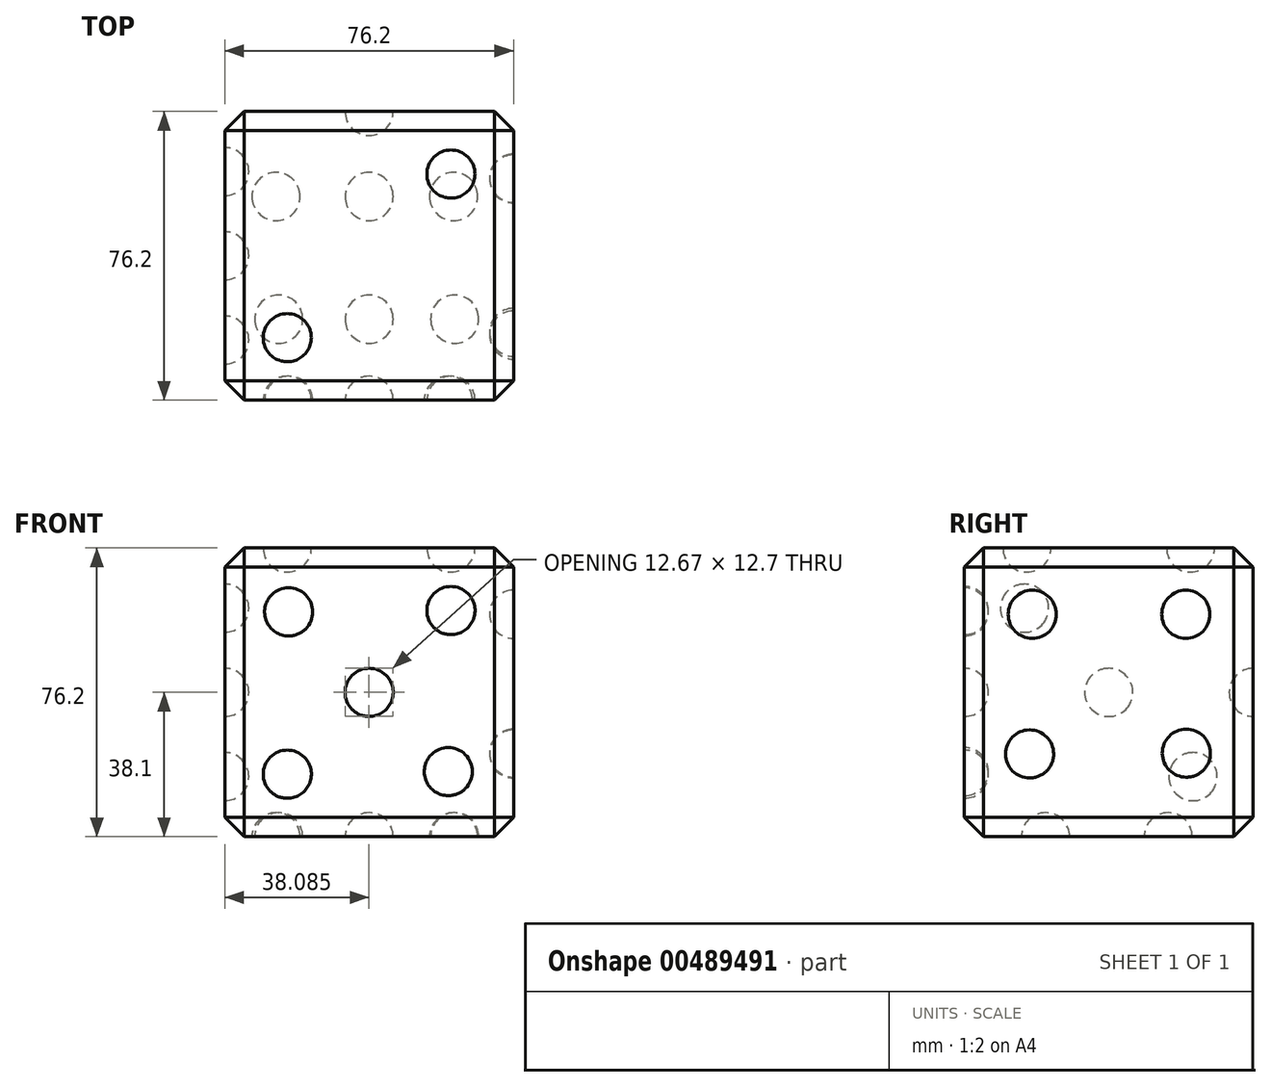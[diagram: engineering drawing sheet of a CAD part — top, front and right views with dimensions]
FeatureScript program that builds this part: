
annotation { "Feature Type Name" : "Feature", "Feature Type Description" : "" }
export const myFeature = defineFeature(function(context is Context, id is Id, definition is map)
    precondition{}
    {
        {
            var Q0;
            Q0=qCreatedBy(makeId("Top.planeOp"),FACE);
            var sketch = newSketch(context, id + "F0", { "sketchPlane" : qUnion([Q0])});
            skLineSegment(sketch, "E0", {"start": v(0, 0) * mm, "end": v(-76.2, 0) * mm});
            skLineSegment(sketch, "E1", {"start": v(-76.2, 0) * mm, "end": v(-76.2, 76.2) * mm});
            skLineSegment(sketch, "E2", {"start": v(-76.2, 76.2) * mm, "end": v(0, 76.2) * mm});
            skLineSegment(sketch, "E3", {"start": v(0, 76.2) * mm, "end": v(0, 0) * mm});
            skSolve(sketch);
        }
        {
            var Q0;
            Q0 = qSketchRegion(id + "F0", true);
            extrude(context, id + "F1", {"entities" : qUnion([Q0]), "depth" : 76.2 * mm});
        }
        {
            var Q0;
            Q0=makeQuery(id+"F1.opExtrude","SWEPT_FACE",FACE,{"disambiguationData":[OSD([sQuery(id+"F0.wireOp",EDGE,"E2")])]});
            var sketch = newSketch(context, id + "F2", { "sketchPlane" : qUnion([Q0])});
            skLineSegment(sketch, "E4", {"start": v(38.1, 0) * mm, "end": v(38.1, 76.2) * mm});
            skArc(sketch, "E5", {"start": v(38.1, 31.75) * mm, "mid": v(44.45, 38.1) * mm, "end": v(38.1, 44.45) * mm});
            skSolve(sketch);
        }
        {
            var Q0;
            {var subQ0=sQuery(id+"F2.wireOp",EDGE,"E5");Q0=makeQuery(id+"F2.imprint","IMPRINT",FACE,{"disambiguationData":[TD([[makeQuery(id+"F2.imprint","IMPRINT",EDGE,{"derivedFrom":subQ0}),1.0]])]});}
            var Q1;
            Q1=sQuery(id+"F2.wireOp",EDGE,"E4");
            revolve(context, id + "F3", {"operationType" : NewBodyOperationType.REMOVE, "entities" : qUnion([Q0]), "axis" : qUnion([Q1]), "revolveType" : RevolveType.FULL, "oppositeDirection" : true});
        }
        {
            var Q0;
            Q0=makeQuery(id+"F1.opExtrude","SWEPT_FACE",FACE,{"disambiguationData":[OSD([sQuery(id+"F0.wireOp",EDGE,"E1")])]});
            var sketch = newSketch(context, id + "F4", { "sketchPlane" : qUnion([Q0])});
            skLineSegment(sketch, "E6", {"start": v(0, 76.2) * mm, "end": v(-76.2, 0) * mm});
            skArc(sketch, "E7", {"start": v(-42.6, 33.6) * mm, "mid": v(-33.6, 33.6) * mm, "end": v(-33.6, 42.6) * mm});
            skArc(sketch, "E8", {"start": v(-64.82, 11.38) * mm, "mid": v(-55.83, 11.38) * mm, "end": v(-55.83, 20.37) * mm});
            skArc(sketch, "E9", {"start": v(-20.37, 55.83) * mm, "mid": v(-11.38, 55.83) * mm, "end": v(-11.38, 64.82) * mm});
            skSolve(sketch);
        }
        {
            var Q0;
            {var subQ0=sQuery(id+"F4.wireOp",EDGE,"E7");Q0=makeQuery(id+"F4.imprint","IMPRINT",FACE,{"disambiguationData":[TD([[makeQuery(id+"F4.imprint","IMPRINT",EDGE,{"derivedFrom":subQ0}),1.0]])]});}
            var Q1;
            {var subQ0=sQuery(id+"F4.wireOp",EDGE,"E9");Q1=makeQuery(id+"F4.imprint","IMPRINT",FACE,{"disambiguationData":[TD([[makeQuery(id+"F4.imprint","IMPRINT",EDGE,{"derivedFrom":subQ0}),1.0]])]});}
            var Q2;
            {var subQ0=sQuery(id+"F4.wireOp",EDGE,"E8");Q2=makeQuery(id+"F4.imprint","IMPRINT",FACE,{"disambiguationData":[TD([[makeQuery(id+"F4.imprint","IMPRINT",EDGE,{"derivedFrom":subQ0}),1.0]])]});}
            var Q3;
            Q3=sQuery(id+"F4.wireOp",EDGE,"E6");
            revolve(context, id + "F5", {"operationType" : NewBodyOperationType.REMOVE, "entities" : qUnion([Q0, Q1, Q2]), "axis" : qUnion([Q3]), "revolveType" : RevolveType.FULL, "oppositeDirection" : true});
        }
        {
            var Q0;
            Q0=makeQuery(id+"F1.opExtrude","CAP_FACE",FACE,{"disambiguationData":[OSD([sQuery(id+"F0.wireOp",EDGE,"E0"),sQuery(id+"F0.wireOp",EDGE,"E1"),sQuery(id+"F0.wireOp",EDGE,"E2"),sQuery(id+"F0.wireOp",EDGE,"E3")])],"isStart":false});
            var sketch = newSketch(context, id + "F6", { "sketchPlane" : qUnion([Q0])});
            skLineSegment(sketch, "E10", {"start": v(0, 0) * mm, "end": v(-76.2, 76.2) * mm});
            skLineSegment(sketch, "E11", {"start": v(-76.2, 0) * mm, "end": v(0, 76.2) * mm});
            skArc(sketch, "E12", {"start": v(-55.2, 21) * mm, "mid": v(-64.18, 21) * mm, "end": v(-64.18, 12.02) * mm});
            skArc(sketch, "E13", {"start": v(-12.02, 12.02) * mm, "mid": v(-12.02, 21) * mm, "end": v(-21, 21) * mm});
            skArc(sketch, "E14", {"start": v(-42.6, 42.6) * mm, "mid": v(-44.45, 38.1) * mm, "end": v(-42.6, 33.6) * mm});
            skArc(sketch, "E15", {"start": v(-12.02, 64.18) * mm, "mid": v(-21, 64.18) * mm, "end": v(-21, 55.2) * mm});
            skArc(sketch, "E16", {"start": v(-55.2, 55.2) * mm, "mid": v(-55.2, 64.18) * mm, "end": v(-64.18, 64.18) * mm});
            skSolve(sketch);
        }
        {
            var Q0;
            {var subQ0=sQuery(id+"F6.wireOp",EDGE,"E12");Q0=makeQuery(id+"F6.imprint","IMPRINT",FACE,{"disambiguationData":[TD([[makeQuery(id+"F6.imprint","IMPRINT",EDGE,{"derivedFrom":subQ0}),1.0]])]});}
            var Q1;
            {var subQ0=sQuery(id+"F6.wireOp",EDGE,"E15");Q1=makeQuery(id+"F6.imprint","IMPRINT",FACE,{"disambiguationData":[TD([[makeQuery(id+"F6.imprint","IMPRINT",EDGE,{"derivedFrom":subQ0}),1.0]])]});}
            var Q2;
            Q2=sQuery(id+"F6.wireOp",EDGE,"E11");
            revolve(context, id + "F7", {"operationType" : NewBodyOperationType.REMOVE, "entities" : qUnion([Q0, Q1]), "axis" : qUnion([Q2]), "revolveType" : RevolveType.FULL, "oppositeDirection" : true});
        }
        {
            var Q0;
            Q0=makeQuery(id+"F1.opExtrude","SWEPT_FACE",FACE,{"disambiguationData":[OSD([sQuery(id+"F0.wireOp",EDGE,"E0")])]});
            var sketch = newSketch(context, id + "F8", { "sketchPlane" : qUnion([Q0])});
            skLineSegment(sketch, "E17", {"start": v(0, 76.2) * mm, "end": v(-76.2, 0) * mm});
            skArc(sketch, "E18", {"start": v(-12.02, 64.18) * mm, "mid": v(-21, 64.18) * mm, "end": v(-21, 55.2) * mm});
            skArc(sketch, "E19", {"start": v(-64.18, 12.02) * mm, "mid": v(-55.2, 12.02) * mm, "end": v(-55.2, 21) * mm});
            skPoint(sketch, "E20.center.orphan", {"position": v(-59.69, 59.7) * mm});
            skPoint(sketch, "E21.start.orphan", {"position": v(-76.2, 76.2) * mm});
            skPoint(sketch, "E22.trimOffspring.end.orphan", {"position": v(-16.5, 16.5) * mm});
            skPoint(sketch, "E23.trimOffspring.end.orphan", {"position": v(0, 0) * mm});
            skPoint(sketch, "E24.center.orphan", {"position": v(-38.1, 38.1) * mm});
            skArc(sketch, "E25", {"start": v(-33.6, 42.6) * mm, "mid": v(-42.6, 42.6) * mm, "end": v(-42.6, 33.6) * mm});
            skLineSegment(sketch, "E26.trimOffspring", {"start": v(-42.6, 42.6) * mm, "end": v(-38.1, 38.1) * mm});
            skSolve(sketch);
        }
        {
            var Q0;
            {var subQ0=sQuery(id+"F8.wireOp",EDGE,"E25");Q0=makeQuery(id+"F8.imprint","IMPRINT",FACE,{"disambiguationData":[TD([[makeQuery(id+"F8.imprint","IMPRINT",EDGE,{"derivedFrom":subQ0}),1.0]])]});}
            var Q1;
            {var subQ0=sQuery(id+"F8.wireOp",EDGE,"E19");Q1=makeQuery(id+"F8.imprint","IMPRINT",FACE,{"disambiguationData":[TD([[makeQuery(id+"F8.imprint","IMPRINT",EDGE,{"derivedFrom":subQ0}),1.0]])]});}
            var Q2;
            {var subQ0=sQuery(id+"F8.wireOp",EDGE,"E18");Q2=makeQuery(id+"F8.imprint","IMPRINT",FACE,{"disambiguationData":[TD([[makeQuery(id+"F8.imprint","IMPRINT",EDGE,{"derivedFrom":subQ0}),1.0]])]});}
            var Q3;
            Q3=sQuery(id+"F8.wireOp",EDGE,"E17");
            revolve(context, id + "F9", {"operationType" : NewBodyOperationType.REMOVE, "entities" : qUnion([Q0, Q1, Q2]), "axis" : qUnion([Q3]), "revolveType" : RevolveType.FULL, "oppositeDirection" : true});
        }
        {
            var Q0;
            Q0=makeQuery(id+"F1.opExtrude","SWEPT_FACE",FACE,{"disambiguationData":[OSD([sQuery(id+"F0.wireOp",EDGE,"E0")])]});
            var sketch = newSketch(context, id + "F10", { "sketchPlane" : qUnion([Q0])});
            skLineSegment(sketch, "E27", {"start": v(-76.2, 76.2) * mm, "end": v(0, 0) * mm});
            skLineSegment(sketch, "E28", {"start": v(0, 0) * mm, "end": v(-0.99, -0.3) * mm});
            skArc(sketch, "E29", {"start": v(-54.86, 54.86) * mm, "mid": v(-54.86, 63.84) * mm, "end": v(-63.84, 63.84) * mm});
            skArc(sketch, "E30", {"start": v(-12.7, 12.7) * mm, "mid": v(-12.7, 21.69) * mm, "end": v(-21.69, 21.69) * mm});
            skSolve(sketch);
        }
        {
            var Q0;
            {var subQ0=sQuery(id+"F10.wireOp",EDGE,"E29");Q0=makeQuery(id+"F10.imprint","IMPRINT",FACE,{"disambiguationData":[TD([[makeQuery(id+"F10.imprint","IMPRINT",EDGE,{"derivedFrom":subQ0}),1.0]])]});}
            var Q1;
            {var subQ0=sQuery(id+"F10.wireOp",EDGE,"E30");Q1=makeQuery(id+"F10.imprint","IMPRINT",FACE,{"disambiguationData":[TD([[makeQuery(id+"F10.imprint","IMPRINT",EDGE,{"derivedFrom":subQ0}),1.0]])]});}
            var Q2;
            Q2=sQuery(id+"F10.wireOp",EDGE,"E27");
            revolve(context, id + "F11", {"operationType" : NewBodyOperationType.REMOVE, "entities" : qUnion([Q0, Q1]), "axis" : qUnion([Q2]), "revolveType" : RevolveType.FULL, "oppositeDirection" : true});
        }
        {
            var Q0;
            Q0=makeQuery(id+"F1.opExtrude","CAP_FACE",FACE,{"disambiguationData":[OSD([sQuery(id+"F0.wireOp",EDGE,"E0"),sQuery(id+"F0.wireOp",EDGE,"E1"),sQuery(id+"F0.wireOp",EDGE,"E2"),sQuery(id+"F0.wireOp",EDGE,"E3")])],"isStart":true});
            var sketch = newSketch(context, id + "F12", { "sketchPlane" : qUnion([Q0])});
            skLineSegment(sketch, "E31", {"start": v(0, -21.4) * mm, "end": v(-76.2, -21.4) * mm});
            skPoint(sketch, "E32.center.orphan", {"position": v(-38.1, -21.4) * mm});
            skArc(sketch, "E33", {"start": v(-31.75, -21.4) * mm, "mid": v(-38.1, -15.06) * mm, "end": v(-44.45, -21.4) * mm});
            skArc(sketch, "E34", {"start": v(-9.17, -21.4) * mm, "mid": v(-15.52, -15.06) * mm, "end": v(-21.87, -21.4) * mm});
            skArc(sketch, "E35", {"start": v(-55.62, -21.4) * mm, "mid": v(-61.97, -15.06) * mm, "end": v(-68.32, -21.4) * mm});
            skSolve(sketch);
        }
        {
            var Q0;
            {var subQ0=sQuery(id+"F12.wireOp",EDGE,"E34");Q0=makeQuery(id+"F12.imprint","IMPRINT",FACE,{"disambiguationData":[TD([[makeQuery(id+"F12.imprint","IMPRINT",EDGE,{"derivedFrom":subQ0}),1.0]])]});}
            var Q1;
            {var subQ0=sQuery(id+"F12.wireOp",EDGE,"E33");Q1=makeQuery(id+"F12.imprint","IMPRINT",FACE,{"disambiguationData":[TD([[makeQuery(id+"F12.imprint","IMPRINT",EDGE,{"derivedFrom":subQ0}),1.0]])]});}
            var Q2;
            {var subQ0=sQuery(id+"F12.wireOp",EDGE,"E35");Q2=makeQuery(id+"F12.imprint","IMPRINT",FACE,{"disambiguationData":[TD([[makeQuery(id+"F12.imprint","IMPRINT",EDGE,{"derivedFrom":subQ0}),1.0]])]});}
            var Q3;
            Q3=sQuery(id+"F12.wireOp",EDGE,"E31");
            revolve(context, id + "F13", {"operationType" : NewBodyOperationType.REMOVE, "entities" : qUnion([Q0, Q1, Q2]), "axis" : qUnion([Q3]), "revolveType" : RevolveType.FULL, "oppositeDirection" : true});
        }
        {
            var Q0;
            Q0=makeQuery(id+"F1.opExtrude","CAP_FACE",FACE,{"disambiguationData":[OSD([sQuery(id+"F0.wireOp",EDGE,"E0"),sQuery(id+"F0.wireOp",EDGE,"E1"),sQuery(id+"F0.wireOp",EDGE,"E2"),sQuery(id+"F0.wireOp",EDGE,"E3")])],"isStart":true});
            var sketch = newSketch(context, id + "F14", { "sketchPlane" : qUnion([Q0])});
            skLineSegment(sketch, "E36", {"start": v(0, -53.77) * mm, "end": v(-76.2, -53.77) * mm});
            skArc(sketch, "E37", {"start": v(-22.15, -53.77) * mm, "mid": v(-15.8, -60.12) * mm, "end": v(-9.45, -53.77) * mm});
            skArc(sketch, "E38", {"start": v(-44.45, -53.77) * mm, "mid": v(-38.1, -60.12) * mm, "end": v(-31.75, -53.77) * mm});
            skArc(sketch, "E39", {"start": v(-69.01, -53.77) * mm, "mid": v(-62.66, -60.12) * mm, "end": v(-56.31, -53.77) * mm});
            skSolve(sketch);
        }
        {
            var Q0;
            {var subQ0=sQuery(id+"F14.wireOp",EDGE,"E37");Q0=makeQuery(id+"F14.imprint","IMPRINT",FACE,{"disambiguationData":[TD([[makeQuery(id+"F14.imprint","IMPRINT",EDGE,{"derivedFrom":subQ0}),1.0]])]});}
            var Q1;
            {var subQ0=sQuery(id+"F14.wireOp",EDGE,"E38");Q1=makeQuery(id+"F14.imprint","IMPRINT",FACE,{"disambiguationData":[TD([[makeQuery(id+"F14.imprint","IMPRINT",EDGE,{"derivedFrom":subQ0}),1.0]])]});}
            var Q2;
            {var subQ0=sQuery(id+"F14.wireOp",EDGE,"E39");Q2=makeQuery(id+"F14.imprint","IMPRINT",FACE,{"disambiguationData":[TD([[makeQuery(id+"F14.imprint","IMPRINT",EDGE,{"derivedFrom":subQ0}),1.0]])]});}
            var Q3;
            Q3=sQuery(id+"F14.wireOp",EDGE,"E36");
            revolve(context, id + "F15", {"operationType" : NewBodyOperationType.REMOVE, "entities" : qUnion([Q0, Q1, Q2]), "axis" : qUnion([Q3]), "revolveType" : RevolveType.FULL, "oppositeDirection" : true});
        }
        {
            var Q0;
            Q0=makeQuery(id+"F1.opExtrude","SWEPT_FACE",FACE,{"disambiguationData":[OSD([sQuery(id+"F0.wireOp",EDGE,"E3")])]});
            var sketch = newSketch(context, id + "F16", { "sketchPlane" : qUnion([Q0])});
            skLineSegment(sketch, "E40", {"start": v(76.2, 58.7) * mm, "end": v(0, 58.7) * mm});
            skArc(sketch, "E41", {"start": v(64.78, 58.7) * mm, "mid": v(58.43, 65.06) * mm, "end": v(52.08, 58.7) * mm});
            skArc(sketch, "E42", {"start": v(24.26, 58.7) * mm, "mid": v(17.91, 65.06) * mm, "end": v(11.56, 58.7) * mm});
            skSolve(sketch);
        }
        {
            var Q0;
            {var subQ0=sQuery(id+"F16.wireOp",EDGE,"E42");Q0=makeQuery(id+"F16.imprint","IMPRINT",FACE,{"disambiguationData":[TD([[makeQuery(id+"F16.imprint","IMPRINT",EDGE,{"derivedFrom":subQ0}),1.0]])]});}
            var Q1;
            {var subQ0=sQuery(id+"F16.wireOp",EDGE,"E41");Q1=makeQuery(id+"F16.imprint","IMPRINT",FACE,{"disambiguationData":[TD([[makeQuery(id+"F16.imprint","IMPRINT",EDGE,{"derivedFrom":subQ0}),1.0]])]});}
            var Q2;
            Q2=sQuery(id+"F16.wireOp",EDGE,"E40");
            revolve(context, id + "F17", {"operationType" : NewBodyOperationType.REMOVE, "entities" : qUnion([Q0, Q1]), "axis" : qUnion([Q2]), "revolveType" : RevolveType.FULL, "oppositeDirection" : true});
        }
        {
            var Q0;
            Q0=makeQuery(id+"F1.opExtrude","SWEPT_FACE",FACE,{"disambiguationData":[OSD([sQuery(id+"F0.wireOp",EDGE,"E3")])]});
            var sketch = newSketch(context, id + "F18", { "sketchPlane" : qUnion([Q0])});
            skLineSegment(sketch, "E43", {"start": v(76.2, 22.15) * mm, "end": v(0, 21.79) * mm});
            skArc(sketch, "E44", {"start": v(52.22, 22.03) * mm, "mid": v(58.6, 15.71) * mm, "end": v(64.92, 22.1) * mm});
            skArc(sketch, "E45", {"start": v(10.86, 21.84) * mm, "mid": v(17.24, 15.52) * mm, "end": v(23.56, 21.9) * mm});
            skSolve(sketch);
        }
        {
            var Q0;
            {var subQ0=sQuery(id+"F18.wireOp",EDGE,"E44");Q0=makeQuery(id+"F18.imprint","IMPRINT",FACE,{"disambiguationData":[TD([[makeQuery(id+"F18.imprint","IMPRINT",EDGE,{"derivedFrom":subQ0}),1.0]])]});}
            var Q1;
            {var subQ0=sQuery(id+"F18.wireOp",EDGE,"E45");Q1=makeQuery(id+"F18.imprint","IMPRINT",FACE,{"disambiguationData":[TD([[makeQuery(id+"F18.imprint","IMPRINT",EDGE,{"derivedFrom":subQ0}),1.0]])]});}
            var Q2;
            Q2=sQuery(id+"F18.wireOp",EDGE,"E43");
            revolve(context, id + "F19", {"operationType" : NewBodyOperationType.REMOVE, "entities" : qUnion([Q0, Q1]), "axis" : qUnion([Q2]), "revolveType" : RevolveType.FULL, "oppositeDirection" : true});
        }
        {
            var Q0;
            Q0=makeQuery(id+"F1.opExtrude","SWEPT_EDGE",EDGE,{"disambiguationData":[OSD([sQuery(id+"F0.wireOp",EDGE,"E1"),sQuery(id+"F0.wireOp",EDGE,"E2")])]});
            var Q1;
            Q1=makeQuery(id+"F1.opExtrude","CAP_EDGE",EDGE,{"disambiguationData":[OSD([sQuery(id+"F0.wireOp",EDGE,"E1")])],"isStart":false});
            var Q2;
            Q2=makeQuery(id+"F1.opExtrude","CAP_EDGE",EDGE,{"disambiguationData":[OSD([sQuery(id+"F0.wireOp",EDGE,"E0")])],"isStart":false});
            var Q3;
            Q3=makeQuery(id+"F1.opExtrude","SWEPT_EDGE",EDGE,{"disambiguationData":[OSD([sQuery(id+"F0.wireOp",EDGE,"E0"),sQuery(id+"F0.wireOp",EDGE,"E1")])]});
            var Q4;
            Q4=makeQuery(id+"F1.opExtrude","CAP_EDGE",EDGE,{"disambiguationData":[OSD([sQuery(id+"F0.wireOp",EDGE,"E2")])],"isStart":false});
            var Q5;
            Q5=makeQuery(id+"F1.opExtrude","SWEPT_EDGE",EDGE,{"disambiguationData":[OSD([sQuery(id+"F0.wireOp",EDGE,"E2"),sQuery(id+"F0.wireOp",EDGE,"E3")])]});
            var Q6;
            Q6=makeQuery(id+"F1.opExtrude","CAP_EDGE",EDGE,{"disambiguationData":[OSD([sQuery(id+"F0.wireOp",EDGE,"E3")])],"isStart":false});
            var Q7;
            Q7=makeQuery(id+"F1.opExtrude","CAP_EDGE",EDGE,{"disambiguationData":[OSD([sQuery(id+"F0.wireOp",EDGE,"E3")])],"isStart":true});
            var Q8;
            Q8=makeQuery(id+"F1.opExtrude","SWEPT_EDGE",EDGE,{"disambiguationData":[OSD([sQuery(id+"F0.wireOp",EDGE,"E0"),sQuery(id+"F0.wireOp",EDGE,"E3")])]});
            var Q9;
            Q9=makeQuery(id+"F1.opExtrude","CAP_EDGE",EDGE,{"disambiguationData":[OSD([sQuery(id+"F0.wireOp",EDGE,"E0")])],"isStart":true});
            var Q10;
            Q10=makeQuery(id+"F1.opExtrude","CAP_EDGE",EDGE,{"disambiguationData":[OSD([sQuery(id+"F0.wireOp",EDGE,"E2")])],"isStart":true});
            var Q11;
            Q11=makeQuery(id+"F1.opExtrude","CAP_EDGE",EDGE,{"disambiguationData":[OSD([sQuery(id+"F0.wireOp",EDGE,"E1")])],"isStart":true});
            chamfer(context, id + "F20", {"entities" : qUnion([Q0, Q1, Q2, Q3, Q4, Q5, Q6, Q7, Q8, Q9, Q10, Q11]), "width" : 5.08 * mm, "tangentPropagation" : true});
        }
    });
